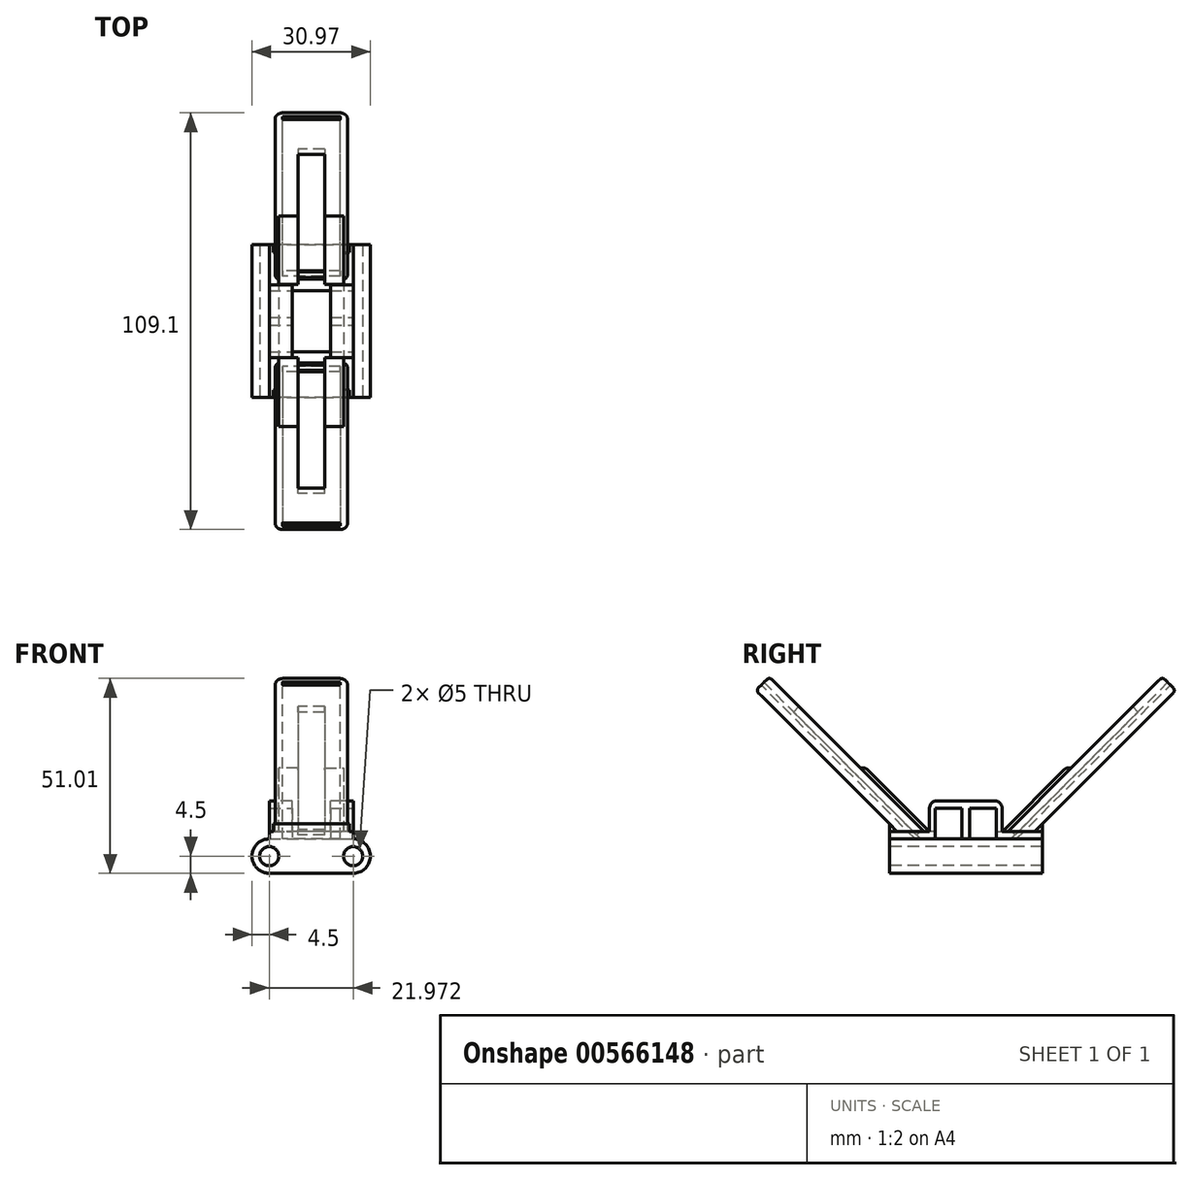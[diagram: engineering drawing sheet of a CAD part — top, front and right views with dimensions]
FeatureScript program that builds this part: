
annotation { "Feature Type Name" : "Feature", "Feature Type Description" : "" }
export const myFeature = defineFeature(function(context is Context, id is Id, definition is map)
    precondition{}
    {
        {
            var Q0;
            Q0=qCreatedBy(makeId("Top.planeOp"),FACE);
            var sketch = newSketch(context, id + "F0", { "sketchPlane" : qUnion([Q0])});
            skLineSegment(sketch, "E0.bottom", {"start": v(-11, 20) * mm, "end": v(11, 20) * mm});
            skLineSegment(sketch, "E0.top", {"start": v(-11, -20) * mm, "end": v(11, -20) * mm});
            skLineSegment(sketch, "E0.left", {"start": v(-11, 20) * mm, "end": v(-11, -20) * mm});
            skLineSegment(sketch, "E0.right", {"start": v(11, 20) * mm, "end": v(11, -20) * mm});
            skPoint(sketch, "E0.middle", {"position": v(0, 0) * mm});
            skSolve(sketch);
        }
        {
            var Q0;
            Q0 = qSketchRegion(id + "F0", true);
            extrude(context, id + "F1", {"entities" : qUnion([Q0]), "oppositeDirection" : true, "depth" : 9 * mm, "offsetDistance" : 25 * mm});
        }
        {
            var Q0;
            Q0=qCreatedBy(makeId("Front.planeOp"),FACE);
            var sketch = newSketch(context, id + "F2", { "sketchPlane" : qUnion([Q0])});
            skCircle(sketch, "E1", {"center": v(-11.03, -4.5) * mm, "radius": 4.5 * mm});
            skPoint(sketch, "E1.first.point", {"position": v(-11, 0) * mm});
            skPoint(sketch, "E1.second.point", {"position": v(-11, -9) * mm});
            skPoint(sketch, "E1.third.point", {"position": v(-15.38, -5.64) * mm});
            skCircle(sketch, "E2", {"center": v(10.94, -4.5) * mm, "radius": 4.5 * mm});
            skPoint(sketch, "E2.first.point", {"position": v(11, 0) * mm});
            skPoint(sketch, "E2.second.point", {"position": v(11, -9) * mm});
            skPoint(sketch, "E2.third.point", {"position": v(6.46, -4.94) * mm});
            skSolve(sketch);
        }
        {
            var Q0;
            Q0 = qSketchRegion(id + "F2", true);
            extrude(context, id + "F3", {"entities" : qUnion([Q0]), "operationType" : NewBodyOperationType.ADD, "endBound" : BoundingType.SYMMETRIC, "oppositeDirection" : true, "depth" : 40 * mm, "offsetDistance" : 25 * mm});
        }
        {
            var Q0;
            Q0=qCreatedBy(makeId("Front.planeOp"),FACE);
            var sketch = newSketch(context, id + "F4", { "sketchPlane" : qUnion([Q0])});
            skCircle(sketch, "E3", {"center": v(-11.03, -4.5) * mm, "radius": 2.5 * mm});
            skCircle(sketch, "E4", {"center": v(10.94, -4.5) * mm, "radius": 2.5 * mm});
            skSolve(sketch);
        }
        {
            var Q0;
            Q0=qCreatedBy(makeId("Top.planeOp"),FACE);
            var sketch = newSketch(context, id + "F5", { "sketchPlane" : qUnion([Q0])});
            skLineSegment(sketch, "E5", {"start": v(-22.5, -9) * mm, "end": v(32.95, -9) * mm});
            skSolve(sketch);
        }
        {
            var Q0;
            Q0=sQuery(id+"F5.wireOp",EDGE,"E5");
            cPlane(context, id + "F6", {"entities" : qUnion([Q0]), "cplaneType" : CPlaneType.LINE_ANGLE, "offset" : 25 * mm, "angle" : 45 * degree, "width" : 150 * mm, "height" : 150 * mm});
        }
        {
            var Q0;
            Q0=qCreatedBy(id+"F6.planeOp",FACE);
            var sketch = newSketch(context, id + "F7", { "sketchPlane" : qUnion([Q0])});
            skLineSegment(sketch, "E6.bottom", {"start": v(9.5, 6.36) * mm, "end": v(-9.5, 6.36) * mm});
            skLineSegment(sketch, "E6.top", {"start": v(9.5, 66.36) * mm, "end": v(-9.5, 66.36) * mm});
            skLineSegment(sketch, "E6.left", {"start": v(9.5, 6.36) * mm, "end": v(9.5, 66.36) * mm});
            skLineSegment(sketch, "E6.right", {"start": v(-9.5, 6.36) * mm, "end": v(-9.5, 66.36) * mm});
            skSolve(sketch);
        }
        {
            var Q0;
            Q0 = qSketchRegion(id + "F7", true);
            extrude(context, id + "F8", {"entities" : qUnion([Q0]), "operationType" : NewBodyOperationType.ADD, "oppositeDirection" : true, "depth" : 5 * mm, "offsetDistance" : 25 * mm});
        }
        {
            var Q0;
            Q0=makeQuery(id+"F8.opExtrude","SWEPT_EDGE",EDGE,{"disambiguationData":[OSD([sQuery(id+"F7.wireOp",EDGE,"E6.top"),sQuery(id+"F7.wireOp",EDGE,"E6.left")])]});
            var Q1;
            Q1=makeQuery(id+"F8.opExtrude","SWEPT_EDGE",EDGE,{"disambiguationData":[OSD([sQuery(id+"F7.wireOp",EDGE,"E6.top"),sQuery(id+"F7.wireOp",EDGE,"E6.right")])]});
            fillet(context, id + "F9", {"entities" : qUnion([Q0, Q1]), "radius" : (2) * mm, "tangentPropagation" : true, "allowEdgeOverflow" : false});
        }
        {
            var Q0;
            Q0=makeQuery(id+"F8.opExtrude","CAP_EDGE",EDGE,{"disambiguationData":[OSD([sQuery(id+"F7.wireOp",EDGE,"E6.right")])],"isStart":true});
            var Q1;
            Q1=makeQuery(id+"F8.opExtrude","CAP_EDGE",EDGE,{"disambiguationData":[OSD([sQuery(id+"F7.wireOp",EDGE,"E6.right")])],"isStart":false});
            var Q2;
            Q2=makeQuery(id+"F8.opExtrude","CAP_EDGE",EDGE,{"disambiguationData":[OSD([sQuery(id+"F7.wireOp",EDGE,"E6.left")])],"isStart":true});
            var Q3;
            Q3=makeQuery(id+"F8.opExtrude","CAP_EDGE",EDGE,{"disambiguationData":[OSD([sQuery(id+"F7.wireOp",EDGE,"E6.left")])],"isStart":false});
            fillet(context, id + "F10", {"entities" : qUnion([Q0, Q1, Q2, Q3]), "radius" : 1 * mm, "tangentPropagation" : true, "allowEdgeOverflow" : false});
        }
        {
            var Q0;
            Q0=qCreatedBy(makeId("Right.planeOp"),FACE);
            var sketch = newSketch(context, id + "F11", { "sketchPlane" : qUnion([Q0])});
            skLineSegment(sketch, "E7.bottom", {"start": v(-9.5, 10) * mm, "end": v(9.5, 10) * mm});
            skLineSegment(sketch, "E7.top", {"start": v(-9.5, 0) * mm, "end": v(9.5, 0) * mm});
            skLineSegment(sketch, "E7.left", {"start": v(-9.5, 10) * mm, "end": v(-9.5, 0) * mm});
            skLineSegment(sketch, "E7.right", {"start": v(9.5, 10) * mm, "end": v(9.5, 0) * mm});
            skSolve(sketch);
        }
        {
            var Q0;
            Q0 = qSketchRegion(id + "F11", true);
            extrude(context, id + "F12", {"entities" : qUnion([Q0]), "operationType" : NewBodyOperationType.ADD, "endBound" : BoundingType.SYMMETRIC, "depth" : 22 * mm, "offsetDistance" : 25 * mm});
        }
        {
            var Q0;
            Q0=makeQuery(id+"F12.opExtrude","SWEPT_EDGE",EDGE,{"disambiguationData":[OSD([sQuery(id+"F11.wireOp",EDGE,"E7.bottom"),sQuery(id+"F11.wireOp",EDGE,"E7.left")])]});
            var Q1;
            Q1=makeQuery(id+"F12.opExtrude","SWEPT_EDGE",EDGE,{"disambiguationData":[OSD([sQuery(id+"F11.wireOp",EDGE,"E7.bottom"),sQuery(id+"F11.wireOp",EDGE,"E7.right")])]});
            fillet(context, id + "F13", {"entities" : qUnion([Q0, Q1]), "radius" : 2 * mm, "tangentPropagation" : true, "allowEdgeOverflow" : false});
        }
        {
            var Q0;
            Q0=qCreatedBy(makeId("Right.planeOp"),FACE);
            var sketch = newSketch(context, id + "F14", { "sketchPlane" : qUnion([Q0])});
            skLineSegment(sketch, "E8.bottom", {"start": v(-8, 0) * mm, "end": v(-1, 0) * mm});
            skLineSegment(sketch, "E8.top", {"start": v(-8, 8) * mm, "end": v(-1, 8) * mm});
            skLineSegment(sketch, "E8.left", {"start": v(-8, 0) * mm, "end": v(-8, 8) * mm});
            skLineSegment(sketch, "E8.right", {"start": v(-1, 0) * mm, "end": v(-1, 8) * mm});
            skLineSegment(sketch, "E9.bottom", {"start": v(8, 0) * mm, "end": v(1, 0) * mm});
            skLineSegment(sketch, "E9.top", {"start": v(8, 8) * mm, "end": v(1, 8) * mm});
            skLineSegment(sketch, "E9.left", {"start": v(8, 0) * mm, "end": v(8, 8) * mm});
            skLineSegment(sketch, "E9.right", {"start": v(1, 0) * mm, "end": v(1, 8) * mm});
            skSolve(sketch);
        }
        {
            var Q0;
            Q0 = qSketchRegion(id + "F14", true);
            extrude(context, id + "F15", {"entities" : qUnion([Q0]), "operationType" : NewBodyOperationType.REMOVE, "endBound" : BoundingType.SYMMETRIC, "oppositeDirection" : true, "depth" : 55 * mm, "offsetDistance" : 25 * mm});
        }
        {
            var Q0;
            Q0=qCreatedBy(makeId("Right.planeOp"),FACE);
            var sketch = newSketch(context, id + "F16", { "sketchPlane" : qUnion([Q0])});
            skLineSegment(sketch, "E10.bottom", {"start": v(-9.5, 0) * mm, "end": v(9.5, 0) * mm});
            skLineSegment(sketch, "E10.top", {"start": v(-9.5, 10) * mm, "end": v(9.5, 10) * mm});
            skLineSegment(sketch, "E10.left", {"start": v(-9.5, 0) * mm, "end": v(-9.5, 10) * mm});
            skLineSegment(sketch, "E10.right", {"start": v(9.5, 0) * mm, "end": v(9.5, 10) * mm});
            skSolve(sketch);
        }
        {
            var Q0;
            Q0 = qSketchRegion(id + "F16", true);
            var Q1;
            Q1 = qSketchRegion(id + "F14", true);
            extrude(context, id + "F17", {"entities" : qUnion([Q0, Q1]), "operationType" : NewBodyOperationType.REMOVE, "endBound" : BoundingType.SYMMETRIC, "oppositeDirection" : true, "depth" : 10 * mm, "offsetDistance" : 25 * mm});
        }
        {
            var Q0;
            Q0=makeQuery(id+"F8.opExtrude","SWEPT_FACE",FACE,{"disambiguationData":[OSD([sQuery(id+"F7.wireOp",EDGE,"E6.top")])]});
            var sketch = newSketch(context, id + "F18", { "sketchPlane" : qUnion([Q0])});
            skLineSegment(sketch, "E11.bottom", {"start": v(-7.6, -8.36) * mm, "end": v(7.6, -8.36) * mm});
            skLineSegment(sketch, "E11.top", {"start": v(-7.6, -9.36) * mm, "end": v(7.6, -9.36) * mm});
            skLineSegment(sketch, "E11.left", {"start": v(-7.6, -8.36) * mm, "end": v(-7.6, -9.36) * mm});
            skLineSegment(sketch, "E11.right", {"start": v(7.6, -8.36) * mm, "end": v(7.6, -9.36) * mm});
            skSolve(sketch);
        }
        {
            var Q0;
            Q0 = qSketchRegion(id + "F18", true);
            extrude(context, id + "F19", {"entities" : qUnion([Q0]), "operationType" : NewBodyOperationType.REMOVE, "oppositeDirection" : true, "depth" : 58.5 * mm, "offsetDistance" : 25 * mm});
        }
        {
            var Q0;
            Q0=makeQuery(id+"F8.opExtrude","CAP_FACE",FACE,{"disambiguationData":[OSD([sQuery(id+"F7.wireOp",EDGE,"E6.bottom"),sQuery(id+"F7.wireOp",EDGE,"E6.top"),sQuery(id+"F7.wireOp",EDGE,"E6.left"),sQuery(id+"F7.wireOp",EDGE,"E6.right")])],"isStart":true});
            var sketch = newSketch(context, id + "F20", { "sketchPlane" : qUnion([Q0])});
            skLineSegment(sketch, "E12.bottom", {"start": v(-3.5, 55.36) * mm, "end": v(3.5, 55.36) * mm});
            skLineSegment(sketch, "E12.top", {"start": v(-3.5, 9.86) * mm, "end": v(3.5, 9.86) * mm});
            skLineSegment(sketch, "E12.left", {"start": v(-3.5, 55.36) * mm, "end": v(-3.5, 9.86) * mm});
            skLineSegment(sketch, "E12.right", {"start": v(3.5, 55.36) * mm, "end": v(3.5, 9.86) * mm});
            skSolve(sketch);
        }
        {
            var Q0;
            Q0 = qSketchRegion(id + "F20", true);
            extrude(context, id + "F21", {"entities" : qUnion([Q0]), "operationType" : NewBodyOperationType.REMOVE, "oppositeDirection" : true, "depth" : 2 * mm, "offsetDistance" : 25 * mm});
        }
        {
            var Q0;
            Q0=qCreatedBy(makeId("Right.planeOp"),FACE);
            var sketch = newSketch(context, id + "F22", { "sketchPlane" : qUnion([Q0])});
            skLineSegment(sketch, "E13", {"start": v(-20, 0) * mm, "end": v(-20, 3.93) * mm});
            skLineSegment(sketch, "E14", {"start": v(-20, 3.93) * mm, "end": v(-16.07, 0) * mm});
            skLineSegment(sketch, "E15", {"start": v(-16.07, 0) * mm, "end": v(-20, 0) * mm});
            skSolve(sketch);
        }
        {
            var Q0;
            Q0 = qSketchRegion(id + "F22", true);
            extrude(context, id + "F23", {"entities" : qUnion([Q0]), "operationType" : NewBodyOperationType.ADD, "endBound" : BoundingType.SYMMETRIC, "depth" : 20 * mm, "offsetDistance" : 25 * mm});
        }
        {
            var Q0;
            Q0=qCreatedBy(makeId("Right.planeOp"),FACE);
            var sketch = newSketch(context, id + "F24", { "sketchPlane" : qUnion([Q0])});
            skLineSegment(sketch, "E16.bottom", {"start": v(-11, 2) * mm, "end": v(-8, 2) * mm});
            skLineSegment(sketch, "E16.top", {"start": v(-11, 0) * mm, "end": v(-8, 0) * mm});
            skLineSegment(sketch, "E16.left", {"start": v(-11, 2) * mm, "end": v(-11, 0) * mm});
            skLineSegment(sketch, "E16.right", {"start": v(-8, 2) * mm, "end": v(-8, 0) * mm});
            skSolve(sketch);
        }
        {
            var Q0;
            Q0 = qSketchRegion(id + "F24", true);
            var Q1;
            Q1 = qSketchRegion(id + "F26", true);
            extrude(context, id + "F25", {"entities" : qUnion([Q0, Q1]), "operationType" : NewBodyOperationType.ADD, "endBound" : BoundingType.SYMMETRIC, "depth" : 22 * mm, "offsetDistance" : 25 * mm});
        }
        {
            var Q0;
            Q0=makeQuery(id+"F3.boolean.opBoolean","MERGE",FACE,{"derivedFrom":[makeQuery(id+"F1.opExtrude","SWEPT_FACE",FACE,{"disambiguationData":[OSD([sQuery(id+"F0.wireOp",EDGE,"E0.top")])]}),makeQuery(id+"F3.opExtrude","CAP_FACE",FACE,{"disambiguationData":[OSD([sQuery(id+"F2.wireOp",EDGE,"E1")])],"isStart":true}),makeQuery(id+"F3.opExtrude","CAP_FACE",FACE,{"disambiguationData":[OSD([sQuery(id+"F2.wireOp",EDGE,"E2")])],"isStart":true})]});
            var sketch = newSketch(context, id + "F26", { "sketchPlane" : qUnion([Q0])});
            skLineSegment(sketch, "E17.bottom", {"start": v(8.5, 2) * mm, "end": v(11, 2) * mm});
            skLineSegment(sketch, "E17.top", {"start": v(8.5, 0) * mm, "end": v(11, 0) * mm});
            skLineSegment(sketch, "E17.left", {"start": v(8.5, 2) * mm, "end": v(8.5, 0) * mm});
            skLineSegment(sketch, "E17.right", {"start": v(11, 2) * mm, "end": v(11, 0) * mm});
            skLineSegment(sketch, "E18.bottom", {"start": v(-11, 2) * mm, "end": v(-8.5, 2) * mm});
            skLineSegment(sketch, "E18.top", {"start": v(-11, 0) * mm, "end": v(-8.5, 0) * mm});
            skLineSegment(sketch, "E18.left", {"start": v(-11, 2) * mm, "end": v(-11, 0) * mm});
            skLineSegment(sketch, "E18.right", {"start": v(-8.5, 2) * mm, "end": v(-8.5, 0) * mm});
            skSolve(sketch);
        }
        {
            var Q0;
            Q0 = qSketchRegion(id + "F26", true);
            extrude(context, id + "F27", {"entities" : qUnion([Q0]), "operationType" : NewBodyOperationType.ADD, "oppositeDirection" : true, "depth" : 11 * mm, "offsetDistance" : 25 * mm});
        }
        {
            var Q0;
            Q0=makeQuery(id+"F1.opExtrude","SWEPT_BODY",BODY,{"disambiguationData":[OSD([sQuery(id+"F0.wireOp",EDGE,"E0.bottom"),sQuery(id+"F0.wireOp",EDGE,"E0.top"),sQuery(id+"F0.wireOp",EDGE,"E0.left"),sQuery(id+"F0.wireOp",EDGE,"E0.right")])]});
            var Q1;
            Q1=qCreatedBy(makeId("Front.planeOp"),FACE);
            mirror(context, id + "F28", {"operationType" : NewBodyOperationType.ADD, "entities" : qUnion([Q0]), "mirrorPlane" : qUnion([Q1])});
        }
        {
            var Q0;
            Q0=makeQuery(id+"F8.opExtrude","CAP_FACE",FACE,{"disambiguationData":[OSD([sQuery(id+"F7.wireOp",EDGE,"E6.bottom"),sQuery(id+"F7.wireOp",EDGE,"E6.top"),sQuery(id+"F7.wireOp",EDGE,"E6.left"),sQuery(id+"F7.wireOp",EDGE,"E6.right")])],"isStart":true});
            var sketch = newSketch(context, id + "F29", { "sketchPlane" : qUnion([Q0])});
            skLineSegment(sketch, "E19.bottom", {"start": v(-3.5, 32.61) * mm, "end": v(-8.5, 32.61) * mm});
            skLineSegment(sketch, "E19.top", {"start": v(-3.5, 7.2) * mm, "end": v(-8.5, 7.2) * mm});
            skLineSegment(sketch, "E19.left", {"start": v(-3.5, 32.61) * mm, "end": v(-3.5, 7.2) * mm});
            skLineSegment(sketch, "E19.right", {"start": v(-8.5, 32.61) * mm, "end": v(-8.5, 7.2) * mm});
            skLineSegment(sketch, "E20.bottom", {"start": v(3.5, 32.61) * mm, "end": v(8.5, 32.61) * mm});
            skLineSegment(sketch, "E20.top", {"start": v(3.5, 7.2) * mm, "end": v(8.5, 7.2) * mm});
            skLineSegment(sketch, "E20.left", {"start": v(3.5, 32.61) * mm, "end": v(3.5, 7.2) * mm});
            skLineSegment(sketch, "E20.right", {"start": v(8.5, 32.61) * mm, "end": v(8.5, 7.2) * mm});
            skSolve(sketch);
        }
        {
            var Q0;
            Q0 = qSketchRegion(id + "F29", true);
            extrude(context, id + "F30", {"entities" : qUnion([Q0]), "operationType" : NewBodyOperationType.ADD, "depth" : 1 * mm, "offsetDistance" : 25 * mm});
        }
        {
            var Q0;
            Q0 = qSketchRegion(id + "F4", true);
            extrude(context, id + "F31", {"entities" : qUnion([Q0]), "operationType" : NewBodyOperationType.REMOVE, "endBound" : BoundingType.SYMMETRIC, "oppositeDirection" : true, "depth" : 40 * mm, "offsetDistance" : 25 * mm});
        }
        {
            var Q0;
            Q0=makeQuery(id+"F1.opExtrude","SWEPT_BODY",BODY,{"disambiguationData":[OSD([sQuery(id+"F0.wireOp",EDGE,"E0.bottom"),sQuery(id+"F0.wireOp",EDGE,"E0.top"),sQuery(id+"F0.wireOp",EDGE,"E0.left"),sQuery(id+"F0.wireOp",EDGE,"E0.right")])]});
            var Q1;
            Q1=qCreatedBy(makeId("Front.planeOp"),FACE);
            mirror(context, id + "F32", {"operationType" : NewBodyOperationType.ADD, "entities" : qUnion([Q0]), "mirrorPlane" : qUnion([Q1])});
        }
        {
            var Q0;
            Q0=makeQuery(id+"F30.opExtrude","CAP_EDGE",EDGE,{"disambiguationData":[OSD([sQuery(id+"F29.wireOp",EDGE,"E20.bottom")])],"isStart":false});
            fillet(context, id + "F33", {"entities" : qUnion([Q0]), "radius" : 2 * mm, "tangentPropagation" : true, "allowEdgeOverflow" : false});
        }
        {
            var Q0;
            Q0=makeQuery(id+"F30.opExtrude","CAP_EDGE",EDGE,{"disambiguationData":[OSD([sQuery(id+"F29.wireOp",EDGE,"E19.bottom")])],"isStart":false});
            fillet(context, id + "F34", {"entities" : qUnion([Q0]), "radius" : 2 * mm, "tangentPropagation" : true, "allowEdgeOverflow" : false});
        }
        {
            var Q0;
            Q0=makeQuery(id+"F32.opPattern","COPY",EDGE,{"derivedFrom":makeQuery(id+"F30.opExtrude","CAP_EDGE",EDGE,{"disambiguationData":[OSD([sQuery(id+"F29.wireOp",EDGE,"E20.bottom")])],"isStart":false}),"instanceName":"1"});
            fillet(context, id + "F35", {"entities" : qUnion([Q0]), "radius" : 2 * mm, "tangentPropagation" : true, "allowEdgeOverflow" : false});
        }
        {
            var Q0;
            Q0=makeQuery(id+"F32.opPattern","COPY",EDGE,{"derivedFrom":makeQuery(id+"F30.opExtrude","CAP_EDGE",EDGE,{"disambiguationData":[OSD([sQuery(id+"F29.wireOp",EDGE,"E19.bottom")])],"isStart":false}),"instanceName":"1"});
            fillet(context, id + "F36", {"entities" : qUnion([Q0]), "radius" : 2 * mm, "tangentPropagation" : true, "allowEdgeOverflow" : false});
        }
    });
